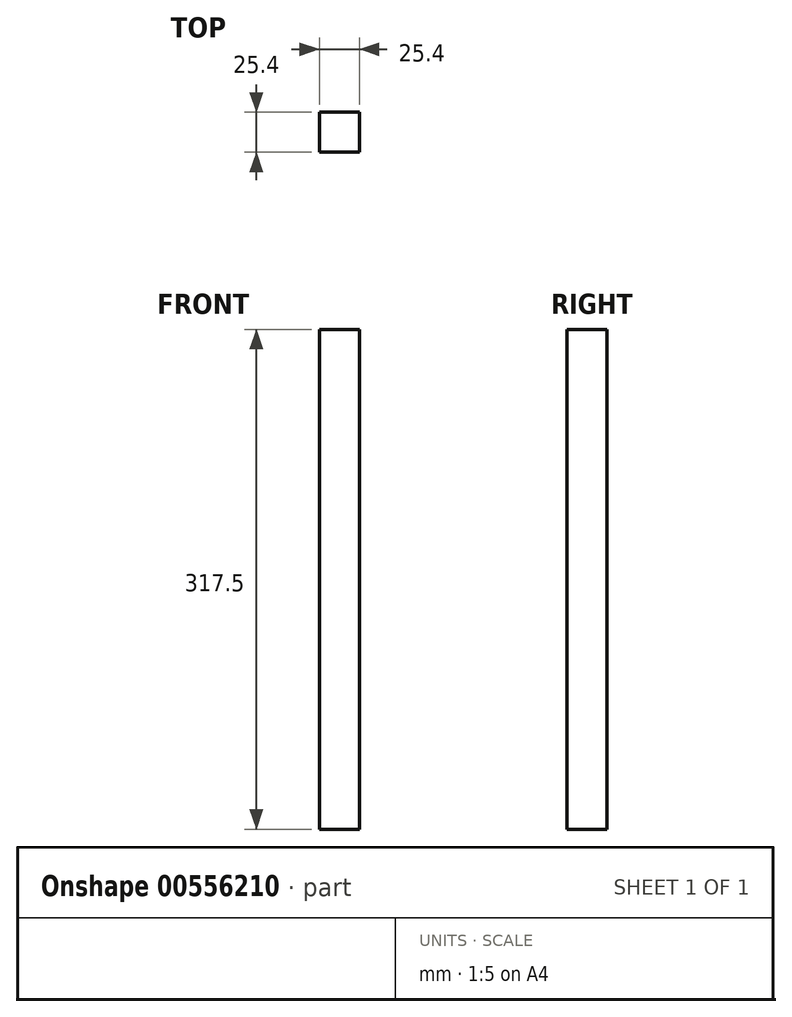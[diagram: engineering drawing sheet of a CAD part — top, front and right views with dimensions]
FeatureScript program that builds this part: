
annotation { "Feature Type Name" : "Feature", "Feature Type Description" : "" }
export const myFeature = defineFeature(function(context is Context, id is Id, definition is map)
    precondition{}
    {
        {
            var Q0;
            Q0=qCreatedBy(makeId("Front.planeOp"),FACE);
            var sketch = newSketch(context, id + "F0", { "sketchPlane" : qUnion([Q0])});
            skLineSegment(sketch, "E0", {"start": v(-12.7, -139.7) * mm, "end": v(12.7, -139.7) * mm});
            skLineSegment(sketch, "E1", {"start": v(12.7, -139.7) * mm, "end": v(12.7, 177.8) * mm});
            skLineSegment(sketch, "E2", {"start": v(12.7, 177.8) * mm, "end": v(-12.7, 177.8) * mm});
            skPoint(sketch, "E3.start.orphan", {"position": v(-12.7, 0) * mm});
            skLineSegment(sketch, "E4", {"start": v(-12.7, 177.8) * mm, "end": v(-12.7, -139.7) * mm});
            skSolve(sketch);
        }
        {
            var Q0;
            Q0 = qSketchRegion(id + "F0", true);
            extrude(context, id + "F1", {"entities" : qUnion([Q0]), "depth" : 25.4 * mm, "offsetDistance" : 25.4 * mm});
        }
    });
